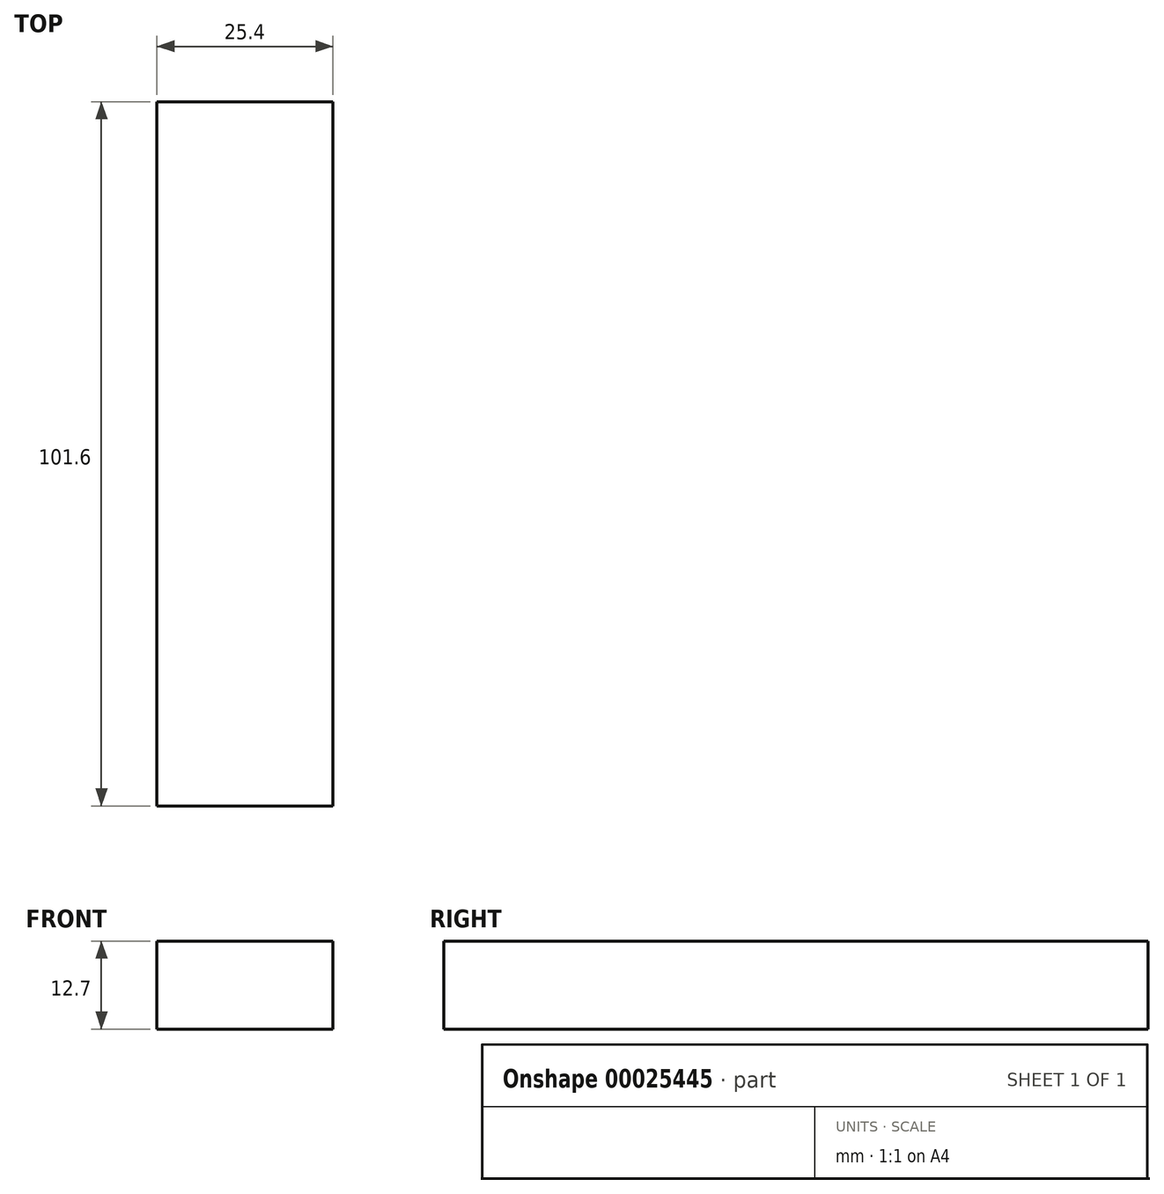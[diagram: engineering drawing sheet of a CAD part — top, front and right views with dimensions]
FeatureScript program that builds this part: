
annotation { "Feature Type Name" : "Feature", "Feature Type Description" : "" }
export const myFeature = defineFeature(function(context is Context, id is Id, definition is map)
    precondition{}
    {
        {
            var Q0;
            Q0=qCreatedBy(makeId("Top.planeOp"),FACE);
            var sketch = newSketch(context, id + "F0", { "sketchPlane" : qUnion([Q0])});
            skLineSegment(sketch, "E0.rect.bottom", {"start": v(12.7, 50.8) * mm, "end": v(-12.7, 50.8) * mm});
            skLineSegment(sketch, "E0.rect.top", {"start": v(12.7, -50.8) * mm, "end": v(-12.7, -50.8) * mm});
            skLineSegment(sketch, "E0.rect.left", {"start": v(12.7, 50.8) * mm, "end": v(12.7, -50.8) * mm});
            skLineSegment(sketch, "E0.rect.right", {"start": v(-12.7, 50.8) * mm, "end": v(-12.7, -50.8) * mm});
            skPoint(sketch, "E0.rect.middle", {"position": v(0, 0) * mm});
            skSolve(sketch);
        }
        {
            var Q0;
            Q0 = qSketchRegion(id + "F0", true);
            extrude(context, id + "F1", {"entities" : qUnion([Q0]), "depth" : 12.7 * mm});
        }
    });
